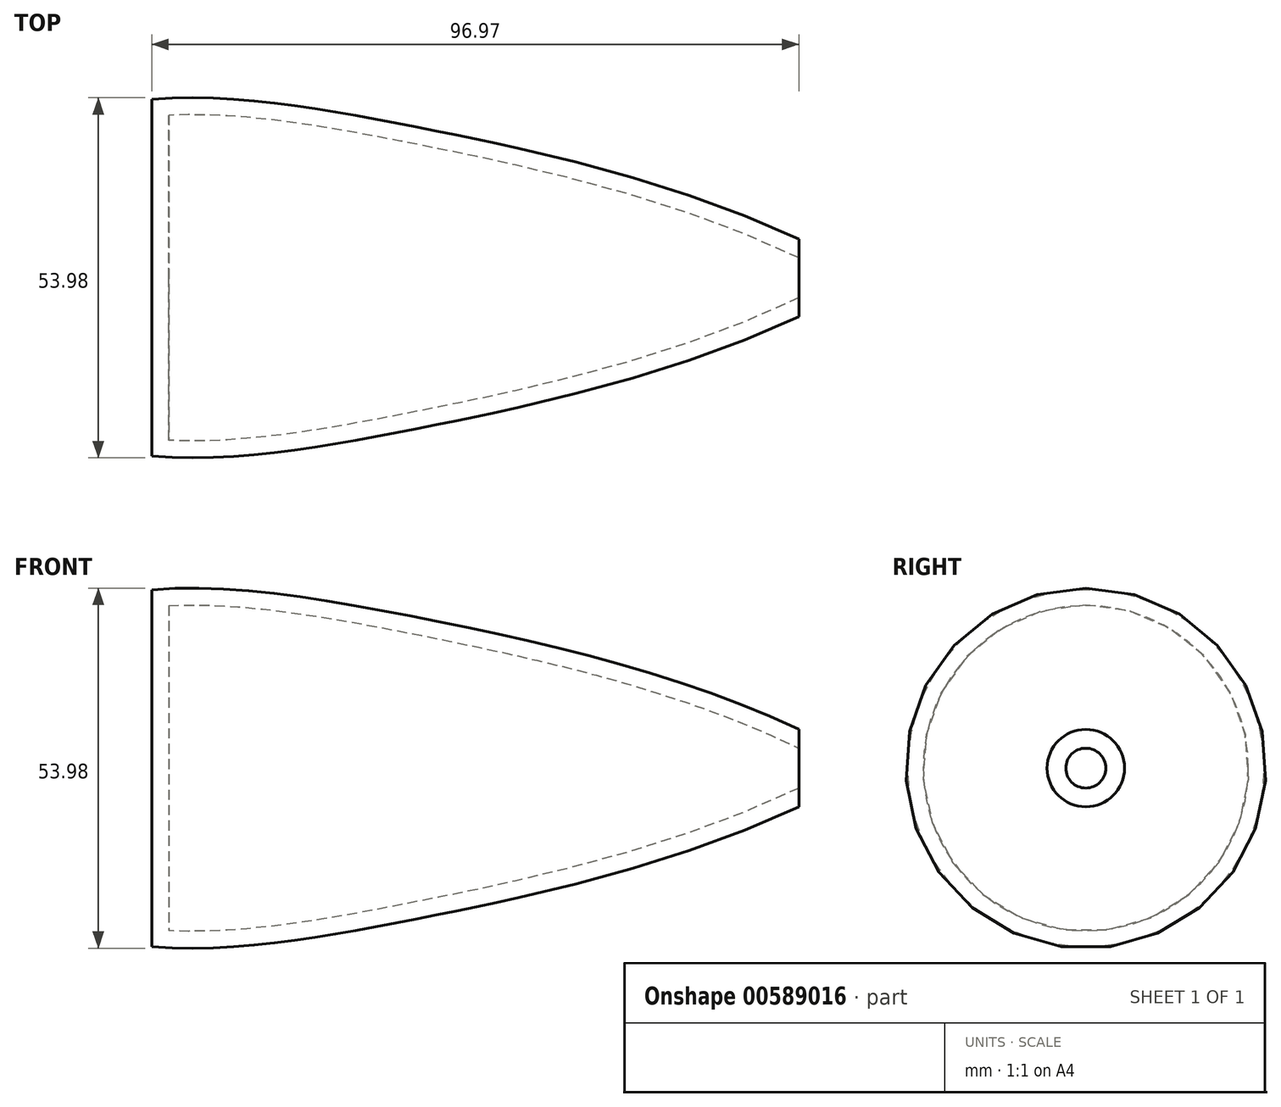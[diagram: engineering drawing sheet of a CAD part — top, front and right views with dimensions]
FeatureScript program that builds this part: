
annotation { "Feature Type Name" : "Feature", "Feature Type Description" : "" }
export const myFeature = defineFeature(function(context is Context, id is Id, definition is map)
    precondition{}
    {
        {
            var Q0;
            Q0=qCreatedBy(makeId("Top.planeOp"),FACE);
            var sketch = newSketch(context, id + "F0", { "sketchPlane" : qUnion([Q0])});
            skLineSegment(sketch, "E0", {"start": v(-40.75, 0) * mm, "end": v(56.22, 0) * mm});
            skLineSegment(sketch, "E1", {"start": v(-40.75, 26.73) * mm, "end": v(-40.75, 0) * mm});
            skLineSegment(sketch, "E2", {"start": v(56.22, 0) * mm, "end": v(56.22, 5.8) * mm});
            skFitSpline(sketch, "E3", {"points": [v(-40.75, 26.73) * mm, v(0, 22.4) * mm, v(56.22, 5.8) * mm], "startDerivative": vector(79.64, 6.93) * mm, "endDerivative": vector(99.13, -46.82) * mm});
            skSolve(sketch);
        }
        {
            var Q0;
            Q0=makeQuery(id+"F0.imprint","IMPRINT",FACE,{"disambiguationData":[TD([[makeQuery(id+"F0.imprint","IMPRINT",EDGE,{"derivedFrom":sQuery(id+"F0.wireOp",EDGE,"E0")}),1.0]])]});
            var Q1;
            Q1=sQuery(id+"F0.wireOp",EDGE,"E0");
            revolve(context, id + "F1", {"entities" : qUnion([Q0]), "axis" : qUnion([Q1]), "revolveType" : RevolveType.FULL});
        }
        {
            var Q0;
            Q0=makeQuery(id+"F1.opRevolve","SWEPT_FACE",FACE,{"disambiguationData":[OSD([sQuery(id+"F0.wireOp",EDGE,"E2")])]});
            shell(context, id + "F2", {"entities" : qUnion([Q0]), "thickness" : 2.54 * mm});
        }
    });
